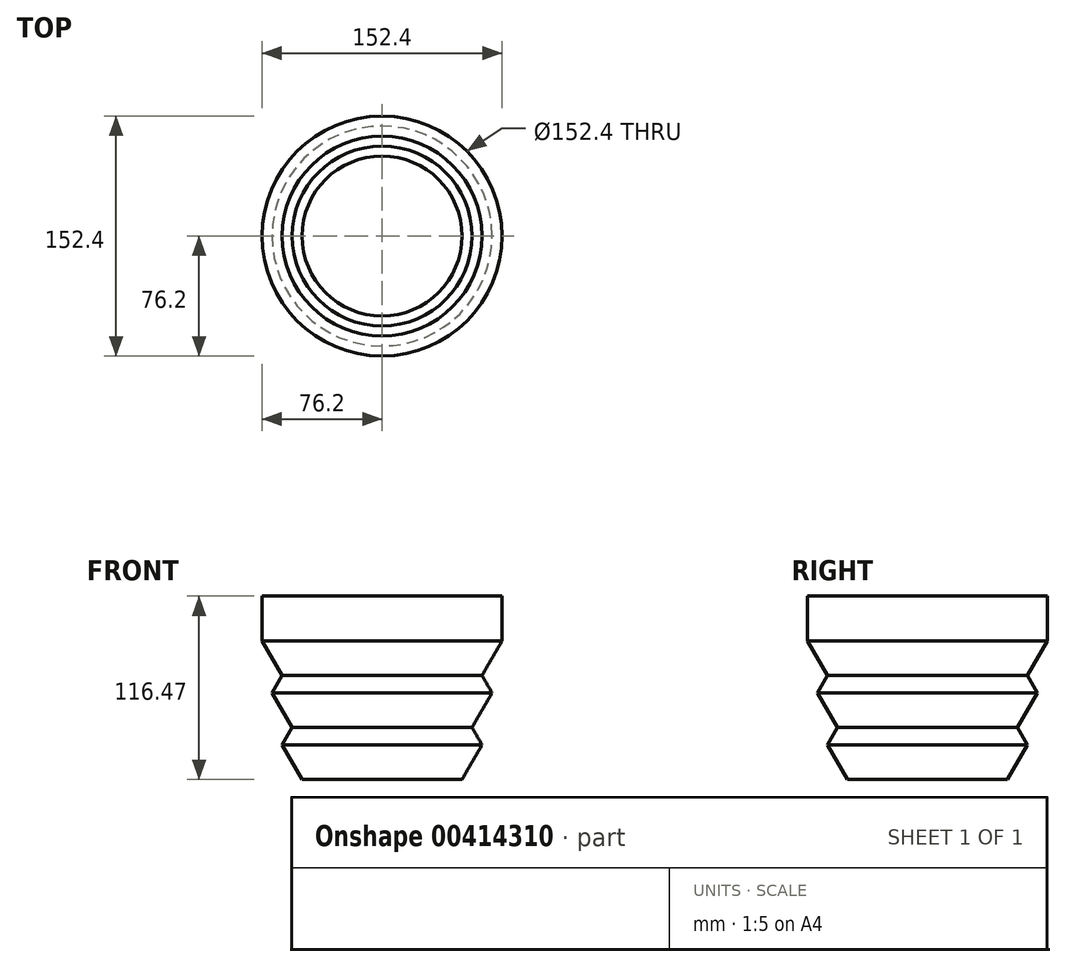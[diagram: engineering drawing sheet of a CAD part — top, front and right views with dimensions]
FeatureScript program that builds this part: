
annotation { "Feature Type Name" : "Feature", "Feature Type Description" : "" }
export const myFeature = defineFeature(function(context is Context, id is Id, definition is map)
    precondition{}
    {
        {
            var Q0;
            Q0=qCreatedBy(makeId("Right.planeOp"),FACE);
            var sketch = newSketch(context, id + "F0", { "sketchPlane" : qUnion([Q0])});
            skLineSegment(sketch, "E0", {"start": v(0, 0) * mm, "end": v(-50.8, 0) * mm});
            skLineSegment(sketch, "E1", {"start": v(-50.8, 0) * mm, "end": v(-63.5, 22) * mm});
            skLineSegment(sketch, "E2", {"start": v(-63.5, 22) * mm, "end": v(-57.15, 33) * mm});
            skLineSegment(sketch, "E3", {"start": v(-57.15, 33) * mm, "end": v(-69.85, 55) * mm});
            skLineSegment(sketch, "E4", {"start": v(-69.85, 55) * mm, "end": v(-63.5, 66) * mm});
            skLineSegment(sketch, "E5", {"start": v(-63.5, 66) * mm, "end": v(-76.2, 87.99) * mm});
            skLineSegment(sketch, "E6", {"start": v(-76.2, 87.99) * mm, "end": v(-76.2, 116.47) * mm});
            skLineSegment(sketch, "E7", {"start": v(0, 0) * mm, "end": v(0, 121.22) * mm, "construction": true});
            skSolve(sketch);
        }
        {
            var Q0;
            Q0=sQuery(id+"F0.wireOp",EDGE,"E5");
            var Q1;
            Q1=sQuery(id+"F0.wireOp",EDGE,"E6");
            var Q2;
            Q2=sQuery(id+"F0.wireOp",EDGE,"E3");
            var Q3;
            Q3=sQuery(id+"F0.wireOp",EDGE,"E1");
            var Q4;
            Q4=sQuery(id+"F0.wireOp",EDGE,"E4");
            var Q5;
            Q5=sQuery(id+"F0.wireOp",EDGE,"E2");
            var Q6;
            Q6=sQuery(id+"F0.wireOp",EDGE,"E0");
            var Q7;
            Q7=sQuery(id+"F0.wireOp",EDGE,"E7");
            revolve(context, id + "F1", {"bodyType" : ToolBodyType.SURFACE, "surfaceEntities" : qUnion([Q0, Q1, Q2, Q3, Q4, Q5, Q6]), "axis" : qUnion([Q7]), "revolveType" : RevolveType.FULL});
        }
    });
